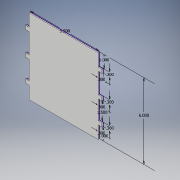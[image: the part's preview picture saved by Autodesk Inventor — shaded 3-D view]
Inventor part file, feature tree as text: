
AUTODESK INVENTOR PART (.ipt)
format: ipt  version: 2018 (Build 220112000, 112)  size: 127,488 bytes
history: native  units: in
note: dims shown in document units (in); Inventor stores cm internally (conversion verified against a paired STEP export)
features: sketch x1, extrude x1
ambient origin geometry x8: Origin, YZ Plane, XZ Plane, XY Plane, X Axis, Y Axis, Z Axis, Center Point
bodies: Solid1 (feature_tree)
feature tree (2):
  sketch  "Sketch1"  dims[d0=5.5in d1=6.0in d2=0.3in d3=0.3in d4=1.0in d5=0.3in d6=0.3in d7=0.3in d8=0.3in d9=1.0in d10=1.5in d11=0.1in d12=0.0in]
  extrude  "Extrusion1"  Depth=6.0in
